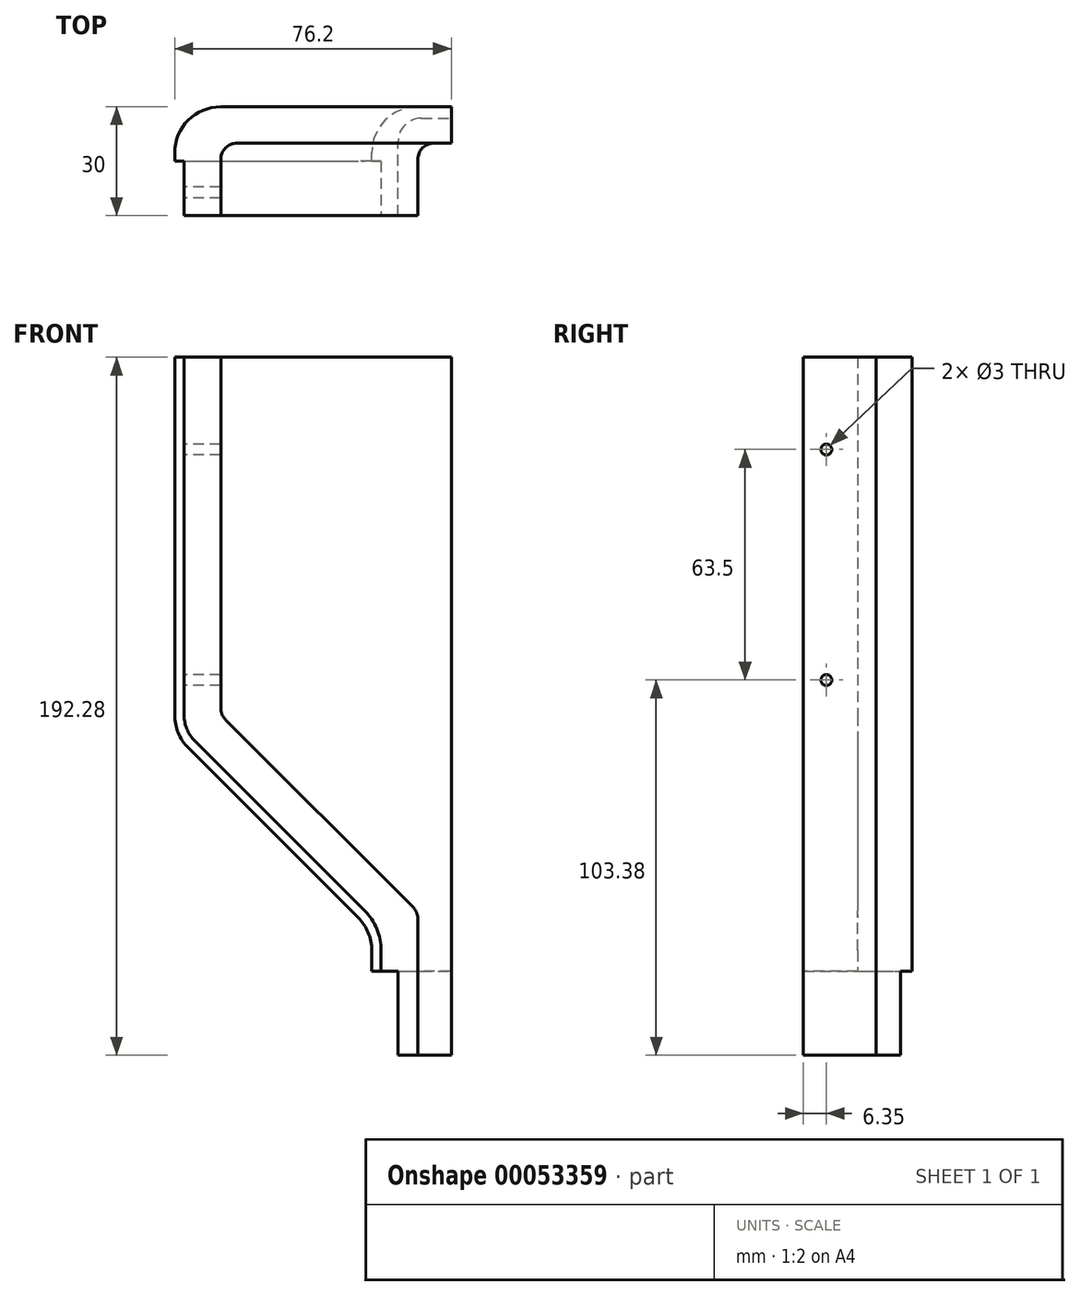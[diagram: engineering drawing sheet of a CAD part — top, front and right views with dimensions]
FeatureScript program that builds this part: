
annotation { "Feature Type Name" : "Feature", "Feature Type Description" : "" }
export const myFeature = defineFeature(function(context is Context, id is Id, definition is map)
    precondition{}
    {
        {
            var Q0;
            Q0=qCreatedBy(makeId("Front.planeOp"),FACE);
            var sketch = newSketch(context, id + "F0", { "sketchPlane" : qUnion([Q0])});
            skLineSegment(sketch, "E0", {"start": v(0, 0) * mm, "end": v(0, 192.28) * mm});
            skLineSegment(sketch, "E1", {"start": v(0, 192.28) * mm, "end": v(-76.2, 192.28) * mm});
            skLineSegment(sketch, "E2", {"start": v(-76.2, 192.28) * mm, "end": v(-76.2, 88.49) * mm});
            skLineSegment(sketch, "E3", {"start": v(-76.2, 88.5) * mm, "end": v(-21.92, 34.2) * mm});
            skLineSegment(sketch, "E4", {"start": v(-21.92, 34.2) * mm, "end": v(-21.92, 22.17) * mm});
            skLineSegment(sketch, "E5", {"start": v(-21.92, 22.17) * mm, "end": v(-15.57, 22.17) * mm});
            skLineSegment(sketch, "E6", {"start": v(-15.57, 22.17) * mm, "end": v(-15.57, 0) * mm});
            skLineSegment(sketch, "E7", {"start": v(-15.57, 0) * mm, "end": v(0, 0) * mm});
            skSolve(sketch);
        }
        {
            var Q0;
            Q0 = qSketchRegion(id + "F0", true);
            extrude(context, id + "F1", {"entities" : qUnion([Q0]), "depth" : 30 * mm});
        }
        {
            var Q0;
            Q0=makeQuery(id+"F1.opExtrude","CAP_FACE",FACE,{"disambiguationData":[OSD([sQuery(id+"F0.wireOp",EDGE,"E0"),sQuery(id+"F0.wireOp",EDGE,"E1"),sQuery(id+"F0.wireOp",EDGE,"E2"),sQuery(id+"F0.wireOp",EDGE,"E3"),sQuery(id+"F0.wireOp",EDGE,"E4"),sQuery(id+"F0.wireOp",EDGE,"E5"),sQuery(id+"F0.wireOp",EDGE,"E6"),sQuery(id+"F0.wireOp",EDGE,"E7")])],"isStart":false});
            var sketch = newSketch(context, id + "F2", { "sketchPlane" : qUnion([Q0])});
            skLineSegment(sketch, "E8", {"start": v(-63.5, 192.28) * mm, "end": v(-63.5, 93.75) * mm});
            skLineSegment(sketch, "E9", {"start": v(-63.5, 93.75) * mm, "end": v(-9.22, 39.47) * mm});
            skLineSegment(sketch, "E10", {"start": v(-9.22, 39.47) * mm, "end": v(-9.22, 0) * mm});
            skLineSegment(sketch, "E11", {"start": v(-9.22, 0) * mm, "end": v(0, 0) * mm});
            skLineSegment(sketch, "E12", {"start": v(0, 0) * mm, "end": v(0, 192.28) * mm});
            skLineSegment(sketch, "E13", {"start": v(0, 192.28) * mm, "end": v(-63.5, 192.28) * mm});
            skSolve(sketch);
        }
        {
            var Q0;
            Q0 = qSketchRegion(id + "F2", true);
            extrude(context, id + "F3", {"entities" : qUnion([Q0]), "operationType" : NewBodyOperationType.REMOVE, "oppositeDirection" : true, "depth" : 20 * mm});
        }
        {
            var Q0;
            Q0=makeQuery(id+"F1.opExtrude","CAP_FACE",FACE,{"disambiguationData":[OSD([sQuery(id+"F0.wireOp",EDGE,"E0"),sQuery(id+"F0.wireOp",EDGE,"E1"),sQuery(id+"F0.wireOp",EDGE,"E2"),sQuery(id+"F0.wireOp",EDGE,"E3"),sQuery(id+"F0.wireOp",EDGE,"E4"),sQuery(id+"F0.wireOp",EDGE,"E5"),sQuery(id+"F0.wireOp",EDGE,"E6"),sQuery(id+"F0.wireOp",EDGE,"E7")])],"isStart":false});
            var sketch = newSketch(context, id + "F4", { "sketchPlane" : qUnion([Q0])});
            skLineSegment(sketch, "E14", {"start": v(-76.2, 192.28) * mm, "end": v(-76.2, 88.5) * mm});
            skLineSegment(sketch, "E15", {"start": v(-76.2, 88.5) * mm, "end": v(-21.92, 34.2) * mm});
            skLineSegment(sketch, "E16", {"start": v(-21.92, 34.2) * mm, "end": v(-21.92, 22.17) * mm});
            skLineSegment(sketch, "E17.0", {"start": v(-19.33, 35.28) * mm, "end": v(-19.33, 22.17) * mm});
            skLineSegment(sketch, "E17.1", {"start": v(-73.61, 89.56) * mm, "end": v(-19.33, 35.28) * mm});
            skLineSegment(sketch, "E17.2", {"start": v(-73.61, 192.28) * mm, "end": v(-73.61, 89.56) * mm});
            skLineSegment(sketch, "E18", {"start": v(-21.92, 22.17) * mm, "end": v(-19.33, 22.17) * mm});
            skLineSegment(sketch, "E19", {"start": v(-76.2, 192.28) * mm, "end": v(-73.61, 192.28) * mm});
            skSolve(sketch);
        }
        {
            var Q0;
            Q0 = qSketchRegion(id + "F4", true);
            extrude(context, id + "F5", {"entities" : qUnion([Q0]), "operationType" : NewBodyOperationType.REMOVE, "oppositeDirection" : true, "depth" : 15 * mm});
        }
        {
            var Q0;
            Q0=makeQuery(id+"F5.boolean.opBoolean","COPY",EDGE,{"derivedFrom":makeQuery(id+"F5.opExtrude","SWEPT_EDGE",EDGE,{"disambiguationData":[OSD([sQuery(id+"F4.wireOp",EDGE,"E17.1"),sQuery(id+"F4.wireOp",EDGE,"E17.2")])]})});
            fillet(context, id + "F6", {"entities" : qUnion([Q0]), "radius" : 10.1 * mm, "tangentPropagation" : true, "allowEdgeOverflow" : false});
        }
        {
            var Q0;
            Q0=makeQuery(id+"F5.boolean.opBoolean","COPY",EDGE,{"derivedFrom":makeQuery(id+"F5.opExtrude","SWEPT_EDGE",EDGE,{"disambiguationData":[OSD([sQuery(id+"F4.wireOp",EDGE,"E17.0"),sQuery(id+"F4.wireOp",EDGE,"E17.1")])]})});
            fillet(context, id + "F7", {"entities" : qUnion([Q0]), "radius" : 15.53 * mm, "tangentPropagation" : true, "allowEdgeOverflow" : false});
        }
        {
            var Q0;
            Q0=makeQuery(id+"F1.opExtrude","SWEPT_EDGE",EDGE,{"disambiguationData":[OSD([sQuery(id+"F0.wireOp",EDGE,"E2"),sQuery(id+"F0.wireOp",EDGE,"E3")])]});
            var Q1;
            Q1=makeQuery(id+"F1.opExtrude","SWEPT_EDGE",EDGE,{"disambiguationData":[OSD([sQuery(id+"F0.wireOp",EDGE,"E3"),sQuery(id+"F0.wireOp",EDGE,"E4")])]});
            fillet(context, id + "F8", {"entities" : qUnion([Q0, Q1]), "radius" : 12.7 * mm, "tangentPropagation" : true, "allowEdgeOverflow" : false});
        }
        {
            var Q0;
            Q0=makeQuery(id+"F1.opExtrude","SWEPT_FACE",FACE,{"disambiguationData":[OSD([sQuery(id+"F0.wireOp",EDGE,"E7")])]});
            var sketch = newSketch(context, id + "F9", { "sketchPlane" : qUnion([Q0])});
            skLineSegment(sketch, "E20", {"start": v(0, 0) * mm, "end": v(-29.3, 0) * mm});
            skLineSegment(sketch, "E21", {"start": v(-29.3, 0) * mm, "end": v(-29.3, 30) * mm});
            skLineSegment(sketch, "E22", {"start": v(-29.3, 30) * mm, "end": v(-14.62, 30) * mm});
            skLineSegment(sketch, "E23", {"start": v(-14.62, 30) * mm, "end": v(-14.62, 3.17) * mm});
            skLineSegment(sketch, "E24", {"start": v(-14.62, 3.17) * mm, "end": v(0, 3.18) * mm});
            skLineSegment(sketch, "E25", {"start": v(0, 3.18) * mm, "end": v(0, 0) * mm});
            skSolve(sketch);
        }
        {
            var Q0;
            Q0 = qSketchRegion(id + "F9", true);
            extrude(context, id + "F10", {"entities" : qUnion([Q0]), "operationType" : NewBodyOperationType.REMOVE, "oppositeDirection" : true, "depth" : 23.1 * mm});
        }
        {
            var Q0;
            Q0=makeQuery(id+"F1.opExtrude","CAP_EDGE",EDGE,{"disambiguationData":[OSD([sQuery(id+"F0.wireOp",EDGE,"E2")])],"isStart":true});
            var Q1;
            {var subQ0=sQuery(id+"F0.wireOp",EDGE,"E3");var subQ1=sQuery(id+"F0.wireOp",EDGE,"E2");Q1=makeQuery(id+"F8.opFillet","BLEND_EDGE",EDGE,{"blendedFrom":[makeQuery(id+"F1.opExtrude","SWEPT_EDGE",EDGE,{"disambiguationData":[OSD([subQ1,subQ0])]}),makeQuery(id+"F1.opExtrude","CAP_FACE",FACE,{"disambiguationData":[OSD([sQuery(id+"F0.wireOp",EDGE,"E0"),sQuery(id+"F0.wireOp",EDGE,"E1"),subQ1,subQ0,sQuery(id+"F0.wireOp",EDGE,"E4"),sQuery(id+"F0.wireOp",EDGE,"E5"),sQuery(id+"F0.wireOp",EDGE,"E6"),sQuery(id+"F0.wireOp",EDGE,"E7")])],"isStart":true})],"blendedInto":[makeQuery(id+"F1.opExtrude","CAP_FACE",FACE,{"disambiguationData":[OSD([sQuery(id+"F0.wireOp",EDGE,"E0"),sQuery(id+"F0.wireOp",EDGE,"E1"),subQ1,subQ0,sQuery(id+"F0.wireOp",EDGE,"E4"),sQuery(id+"F0.wireOp",EDGE,"E5"),sQuery(id+"F0.wireOp",EDGE,"E6"),sQuery(id+"F0.wireOp",EDGE,"E7")])],"isStart":true})]});}
            var Q2;
            Q2=makeQuery(id+"F1.opExtrude","CAP_EDGE",EDGE,{"disambiguationData":[OSD([sQuery(id+"F0.wireOp",EDGE,"E3")])],"isStart":true});
            var Q3;
            {var subQ0=sQuery(id+"F0.wireOp",EDGE,"E4");var subQ1=sQuery(id+"F0.wireOp",EDGE,"E3");Q3=makeQuery(id+"F8.opFillet","BLEND_EDGE",EDGE,{"blendedFrom":[makeQuery(id+"F1.opExtrude","SWEPT_EDGE",EDGE,{"disambiguationData":[OSD([subQ1,subQ0])]}),makeQuery(id+"F1.opExtrude","CAP_FACE",FACE,{"disambiguationData":[OSD([sQuery(id+"F0.wireOp",EDGE,"E0"),sQuery(id+"F0.wireOp",EDGE,"E1"),sQuery(id+"F0.wireOp",EDGE,"E2"),subQ1,subQ0,sQuery(id+"F0.wireOp",EDGE,"E5"),sQuery(id+"F0.wireOp",EDGE,"E6"),sQuery(id+"F0.wireOp",EDGE,"E7")])],"isStart":true})],"blendedInto":[makeQuery(id+"F1.opExtrude","CAP_FACE",FACE,{"disambiguationData":[OSD([sQuery(id+"F0.wireOp",EDGE,"E0"),sQuery(id+"F0.wireOp",EDGE,"E1"),sQuery(id+"F0.wireOp",EDGE,"E2"),subQ1,subQ0,sQuery(id+"F0.wireOp",EDGE,"E5"),sQuery(id+"F0.wireOp",EDGE,"E6"),sQuery(id+"F0.wireOp",EDGE,"E7")])],"isStart":true})]});}
            var Q4;
            Q4=makeQuery(id+"F1.opExtrude","CAP_EDGE",EDGE,{"disambiguationData":[OSD([sQuery(id+"F0.wireOp",EDGE,"E4")])],"isStart":true});
            fillet(context, id + "F11", {"entities" : qUnion([Q0, Q1, Q2, Q3, Q4]), "radius" : 12.7 * mm, "tangentPropagation" : true, "allowEdgeOverflow" : false});
        }
        {
            var Q0;
            Q0=makeQuery(id+"F10.boolean.opBoolean","COPY",EDGE,{"derivedFrom":makeQuery(id+"F10.opExtrude","SWEPT_EDGE",EDGE,{"disambiguationData":[OSD([sQuery(id+"F9.wireOp",EDGE,"E23"),sQuery(id+"F9.wireOp",EDGE,"E24")])]})});
            fillet(context, id + "F12", {"entities" : qUnion([Q0]), "radius" : 6.35 * mm, "tangentPropagation" : true, "allowEdgeOverflow" : false});
        }
        {
            var Q0;
            Q0=makeQuery(id+"F3.boolean.opBoolean","COPY",EDGE,{"derivedFrom":makeQuery(id+"F3.opExtrude","CAP_EDGE",EDGE,{"disambiguationData":[OSD([sQuery(id+"F2.wireOp",EDGE,"E10")])],"isStart":false})});
            var Q1;
            Q1=makeQuery(id+"F3.boolean.opBoolean","COPY",EDGE,{"derivedFrom":makeQuery(id+"F3.opExtrude","CAP_EDGE",EDGE,{"disambiguationData":[OSD([sQuery(id+"F2.wireOp",EDGE,"E9")])],"isStart":false})});
            var Q2;
            Q2=makeQuery(id+"F3.boolean.opBoolean","COPY",EDGE,{"derivedFrom":makeQuery(id+"F3.opExtrude","CAP_EDGE",EDGE,{"disambiguationData":[OSD([sQuery(id+"F2.wireOp",EDGE,"E8")])],"isStart":false})});
            var Q3;
            Q3=makeQuery(id+"F3.boolean.opBoolean","COPY",EDGE,{"derivedFrom":makeQuery(id+"F3.opExtrude","SWEPT_EDGE",EDGE,{"disambiguationData":[OSD([sQuery(id+"F2.wireOp",EDGE,"E8"),sQuery(id+"F2.wireOp",EDGE,"E9")])]})});
            var Q4;
            Q4=makeQuery(id+"F3.boolean.opBoolean","COPY",EDGE,{"derivedFrom":makeQuery(id+"F3.opExtrude","SWEPT_EDGE",EDGE,{"disambiguationData":[OSD([sQuery(id+"F2.wireOp",EDGE,"E9"),sQuery(id+"F2.wireOp",EDGE,"E10")])]})});
            fillet(context, id + "F13", {"entities" : qUnion([Q0, Q1, Q2, Q3, Q4]), "radius" : 4.53 * mm, "tangentPropagation" : true, "allowEdgeOverflow" : false});
        }
        {
            var Q0;
            Q0=makeQuery(id+"F5.boolean.opBoolean","COPY",FACE,{"derivedFrom":makeQuery(id+"F5.opExtrude","SWEPT_FACE",FACE,{"disambiguationData":[OSD([sQuery(id+"F4.wireOp",EDGE,"E17.2")])]})});
            var sketch = newSketch(context, id + "F14", { "sketchPlane" : qUnion([Q0])});
            skCircle(sketch, "E26", {"center": v(23.65, 166.88) * mm, "radius": 1.5 * mm});
            skCircle(sketch, "E27", {"center": v(23.65, 103.38) * mm, "radius": 1.5 * mm});
            skSolve(sketch);
        }
        {
            var Q0;
            Q0 = qSketchRegion(id + "F14", true);
            extrude(context, id + "F15", {"entities" : qUnion([Q0]), "operationType" : NewBodyOperationType.REMOVE, "endBound" : BoundingType.THROUGH_ALL, "oppositeDirection" : true, "depth" : 25 * mm});
        }
        {
            var Q0;
            Q0=makeQuery(id+"F5.boolean.opBoolean","COPY",FACE,{"derivedFrom":makeQuery(id+"F5.opExtrude","SWEPT_FACE",FACE,{"disambiguationData":[OSD([sQuery(id+"F4.wireOp",EDGE,"E17.1")])]})});
            var sketch = newSketch(context, id + "F16", { "sketchPlane" : qUnion([Q0])});
            skCircle(sketch, "E28", {"center": v(-99.28, 23.65) * mm, "radius": 1.5 * mm});
            skCircle(sketch, "E29", {"center": v(-61.18, 23.65) * mm, "radius": 1.5 * mm});
            skSolve(sketch);
        }
        {
            var Q0;
            Q0 = qSketchRegion(id + "F16", true);
            extrude(context, id + "F17", {"entities" : qUnion([Q0]), "operationType" : NewBodyOperationType.REMOVE, "endBound" : BoundingType.THROUGH_ALL, "oppositeDirection" : true, "depth" : 25 * mm});
        }
    });
